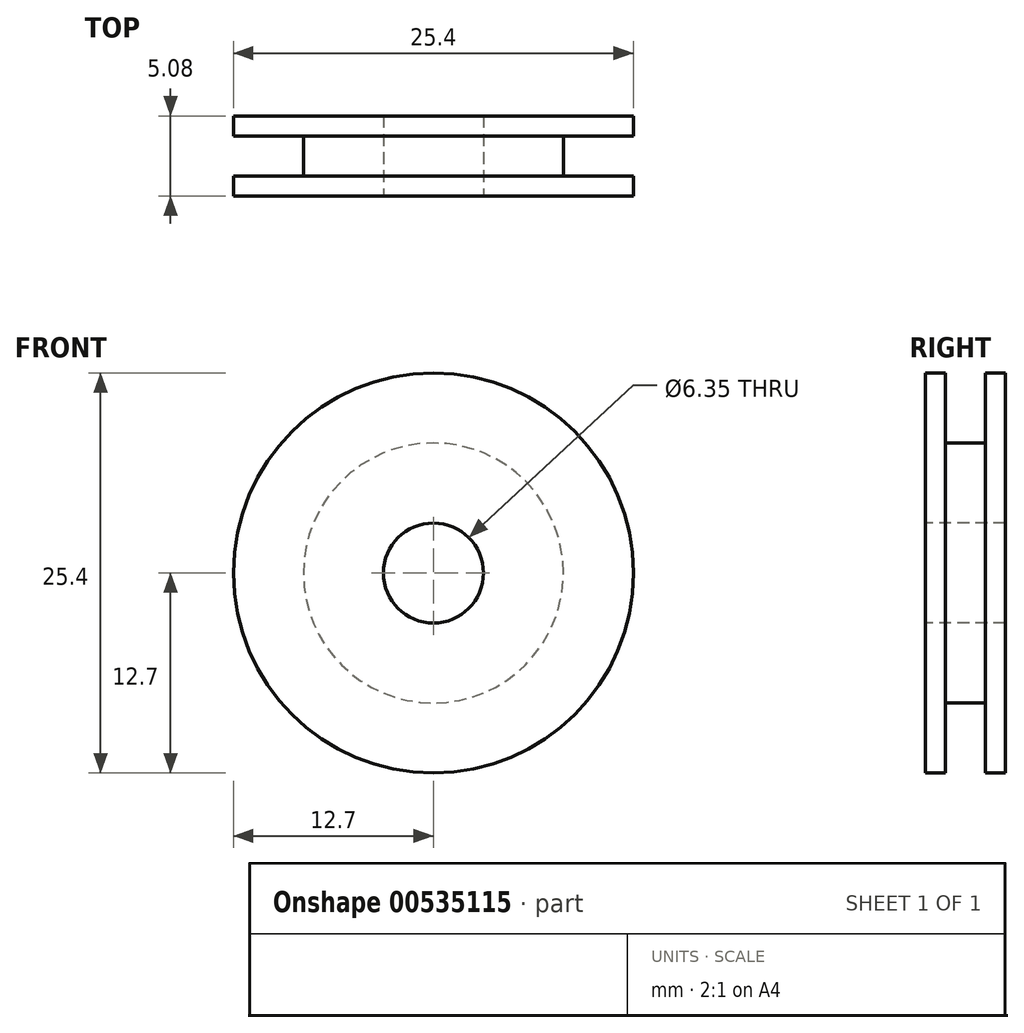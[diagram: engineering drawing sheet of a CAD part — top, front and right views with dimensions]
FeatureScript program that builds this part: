
annotation { "Feature Type Name" : "Feature", "Feature Type Description" : "" }
export const myFeature = defineFeature(function(context is Context, id is Id, definition is map)
    precondition{}
    {
        {
            var Q0;
            Q0=qCreatedBy(makeId("Front.planeOp"),FACE);
            var sketch = newSketch(context, id + "F0", { "sketchPlane" : qUnion([Q0])});
            skCircle(sketch, "E0", {"center": v(0, 0) * mm, "radius": 12.7 * mm});
            skSolve(sketch);
        }
        {
            var Q0;
            Q0=qSketchRegion(id+"F0",true);
            extrude(context, id + "F1", {"entities" : qUnion([Q0]), "depth" : 1.27 * mm});
        }
        {
            var Q0;
            Q0=makeQuery(id+"F1.opExtrude","CAP_FACE",FACE,{"disambiguationData":[OSD([sQuery(id+"F0.wireOp",EDGE,"E0")])],"isStart":false});
            var sketch = newSketch(context, id + "F2", { "sketchPlane" : qUnion([Q0])});
            skCircle(sketch, "E1", {"center": v(0, 0) * mm, "radius": 8.26 * mm});
            skSolve(sketch);
        }
        {
            var Q0;
            Q0=makeQuery(id+"F2.imprint","IMPRINT",FACE,{"disambiguationData":[TD([[makeQuery(id+"F2.imprint","IMPRINT",EDGE,{"derivedFrom":sQuery(id+"F2.wireOp",EDGE,"E1")}),1.0]])]});
            extrude(context, id + "F3", {"entities" : qUnion([Q0]), "operationType" : NewBodyOperationType.ADD, "depth" : 2.54 * mm});
        }
        {
            var Q0;
            Q0=makeQuery(id+"F3.opExtrude","CAP_FACE",FACE,{"disambiguationData":[OSD([sQuery(id+"F2.wireOp",EDGE,"E1")])],"isStart":false});
            var sketch = newSketch(context, id + "F4", { "sketchPlane" : qUnion([Q0])});
            skCircle(sketch, "E2", {"center": v(0, 0) * mm, "radius": 12.7 * mm});
            skSolve(sketch);
        }
        {
            var Q0;
            Q0=qSketchRegion(id+"F4",true);
            extrude(context, id + "F5", {"entities" : qUnion([Q0]), "operationType" : NewBodyOperationType.ADD, "depth" : 1.27 * mm});
        }
        {
            var Q0;
            Q0=makeQuery(id+"F5.opExtrude","CAP_FACE",FACE,{"disambiguationData":[OSD([sQuery(id+"F4.wireOp",EDGE,"E2")])],"isStart":false});
            var sketch = newSketch(context, id + "F6", { "sketchPlane" : qUnion([Q0])});
            skCircle(sketch, "E3", {"center": v(0, 0) * mm, "radius": 3.18 * mm});
            skSolve(sketch);
        }
        {
            var Q0;
            Q0=qSketchRegion(id+"F6",true);
            extrude(context, id + "F7", {"entities" : qUnion([Q0]), "operationType" : NewBodyOperationType.REMOVE, "oppositeDirection" : true, "depth" : 25.4 * mm});
        }
    });
